# Revit family: Time Compact
name_source: partatom
category: Attrezzatura meccanica
units: mm (PartAtom-declared; Revit-internal decimal feet)

## family parameters
Basato su piano di lavoro = No
Classificazione = Nessuno
Condiviso = No
Mantieni orientamento annotazione = No
Punto di calcolo locali = No
Quota connettore circolare = Usa diametro
Sempre verticale = Sì
Taglio con vuoti quando caricato = No
Tipo di parte = Normale

## types (1)
- Time Compact 35 K
    Combustion air inlet - separate system = 80 mm  [stored 0.262467 ft]
    Date of publishing = 15/03/2024
    Depth = 600 mm
    Design country = Italy
    Domestic Cold Water Diameter = 21 mm  [stored 0.0688976 ft]
    Domestic Hot Water Diameter = 21 mm  [stored 0.0688976 ft]
    Efficiency 30% = 107,60%
    Flue outlet = 100 mm  [stored 0.328084 ft]
    Gas Inlet Diameter = 26 mm
    Height = 1750 mm  [stored 5.74147 ft]
    Hydronic Return Diameter = 26 mm
    Hydronic Supply Diameter = 26 mm
    IFC Classification = Boiler
    Manufacturer country = Italy
    Manufacturer name = Italtherm S.p.A.
    Material main = Metal
    Material secondary = Plastic
    Maximum heat output 50/30°C = 34700 W
    Maximum heat output 80/60°C = 32000 W
    Maximum heating heat input = 33000 W
    Minimum heat output 50/30°C = 3600 W
    Minimum heat output 80/60°C = 3200 W
    NBS reference Description = Boilers
    Nominal efficiency 50/30°C = 105,10%
    Nominal efficiency 80/60°C = 97,00%
    Omniclass Description = Condensing boilers
    Power consumption (W) = 100 W
    Power supply | Frequency (Hz) = 50 Hz
    Power supply | Phase = 1
    Power supply | Voltage (V) = 230 V
    Product family = Heating
    Product group = Thermal unit
    Prospetto di default = 0 mm  [stored 0 ft]
    Siphon with condensate drain = 25 mm  [stored 0.082021 ft]
    Uniclass 2015 Name = Boilers
    Weight = 149,00 kg
    Width = 600 mm

note: [stored X ft] marks values corroborated as IEEE doubles in the binary element streams (Revit-internal decimal feet)
